# Revit family: EDLR-E2-235-xxxx-8xx-WS-EL
name_source: partatom
category: Leuchten
revit_build: Autodesk Revit 2017 (Build: 20190508_0315(x64)
units: mm (PartAtom-declared; Revit-internal decimal feet)

## family parameters
Basisbauteil = Fläche
Beim Laden mit Abzugskörper schneiden = Ja
Bemaßung runder Anschluss = Durchmesser verwenden
Gemeinsam genutzt = Nein
Lichtquelle = Ja
OmniClass-Nummer = 23.80.70.11
OmniClass-Titel = Luminaries for Internal Lighting
Raumberechnungspunkt = Nein
Teiletyp = Normal

## types (4) — shared parameters
Baugruppenkennzeichen = D5020200
Datei für fotometrisches Netz = EDLR-E2 235_2000-840 WS.IES
Emissionsform beim Rendern sichtbar = Nein
Farbfilter = 16777215
Farbtemperaturverschiebung bei Dämpfen der Lampe = <Keine Auswahl>
Hersteller = RIDI Leuchten GmbH
Lampe = LED
Neigungswinkel = 90.00°
URL = www.ridi.de
Von Kreisdurchmesser aussenden = 215 mm
brand = RIDI
conformity mark = CE
electrical safety class = 1
height = 75 mm
ingress protection (IP) code = IP20
length = 235 mm  [stored 0.770997 ft]
nominal frequency = 50-60Hz
nominal voltage = 230
voltage type (AC, DC, UC) = AC
width = 235 mm  [stored 0.770997 ft]
zero-valued in all types: Vorgabe-Ansicht

## per-type parameters (varying)
| type | Modell | Scheinlast | rated input power | weight |
| EDLR-E2 235/1100-830 WS-EL | 0326653 | 9 VA | 9 | 0,493kg |
| EDLR-E2 235/1100-840 WS-EL | 0326652 | 9 VA | 9 | 0,493kg |
| EDLR-E2 235/2000-830 WS-EL | 0326655 | 16 VA | 16 | 0,535kg |
| EDLR-E2 235/2000-840 WS-EL | 0326654 | 16 VA | 16 | 0,535kg |

note: column(s) folded — value = type name in every type: product name

note: [stored X ft] marks values corroborated as IEEE doubles in the binary element streams (Revit-internal decimal feet)
